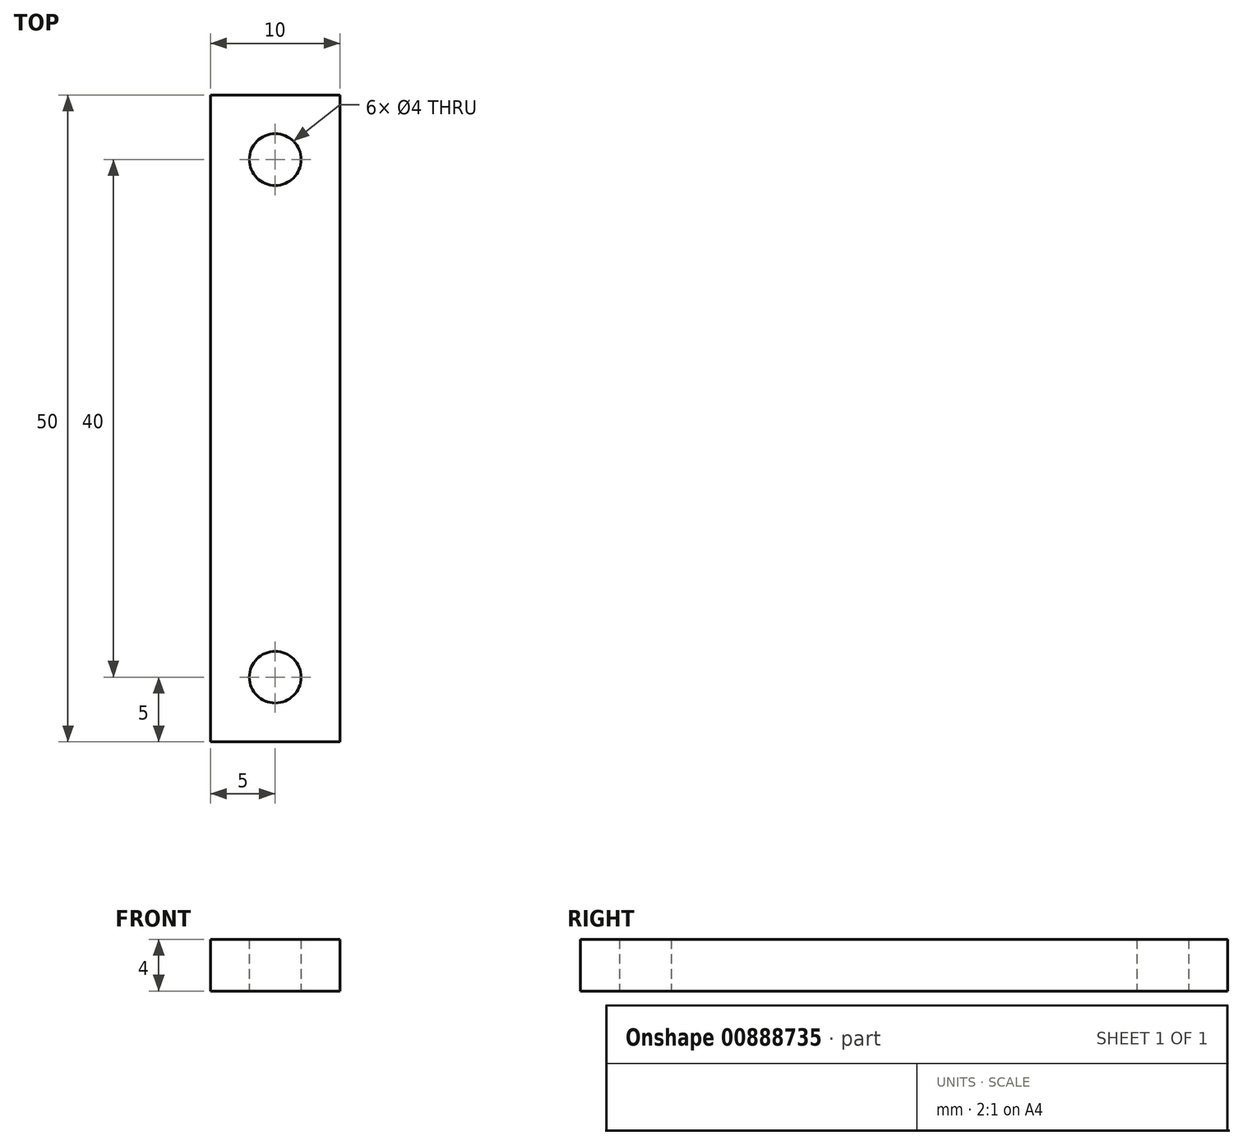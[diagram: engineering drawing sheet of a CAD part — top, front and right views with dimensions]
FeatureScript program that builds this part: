
annotation { "Feature Type Name" : "Feature", "Feature Type Description" : "" }
export const myFeature = defineFeature(function(context is Context, id is Id, definition is map)
    precondition{}
    {
        {
            var Q0;
            Q0=qCreatedBy(makeId("Top.planeOp"),FACE);
            var sketch = newSketch(context, id + "F0", { "sketchPlane" : qUnion([Q0])});
            skCircle(sketch, "E0", {"center": v(0, 0) * mm, "radius": 2 * mm});
            skCircle(sketch, "E1", {"center": v(0, 40) * mm, "radius": 2 * mm});
            skLineSegment(sketch, "E2.bottom", {"start": v(-5, 45) * mm, "end": v(5, 45) * mm});
            skLineSegment(sketch, "E2.top", {"start": v(-5, -5) * mm, "end": v(5, -5) * mm});
            skLineSegment(sketch, "E2.left", {"start": v(-5, 45) * mm, "end": v(-5, -5) * mm});
            skLineSegment(sketch, "E2.right", {"start": v(5, 45) * mm, "end": v(5, -5) * mm});
            skPoint(sketch, "E3", {"position": v(0, -5) * mm});
            skSolve(sketch);
        }
        {
            var Q0;
            Q0 = qSketchRegion(id + "F0", true);
            extrude(context, id + "F1", {"entities" : qUnion([Q0]), "endBound" : BoundingType.SYMMETRIC, "depth" : 4 * mm, "offsetDistance" : 25 * mm});
        }
    });
